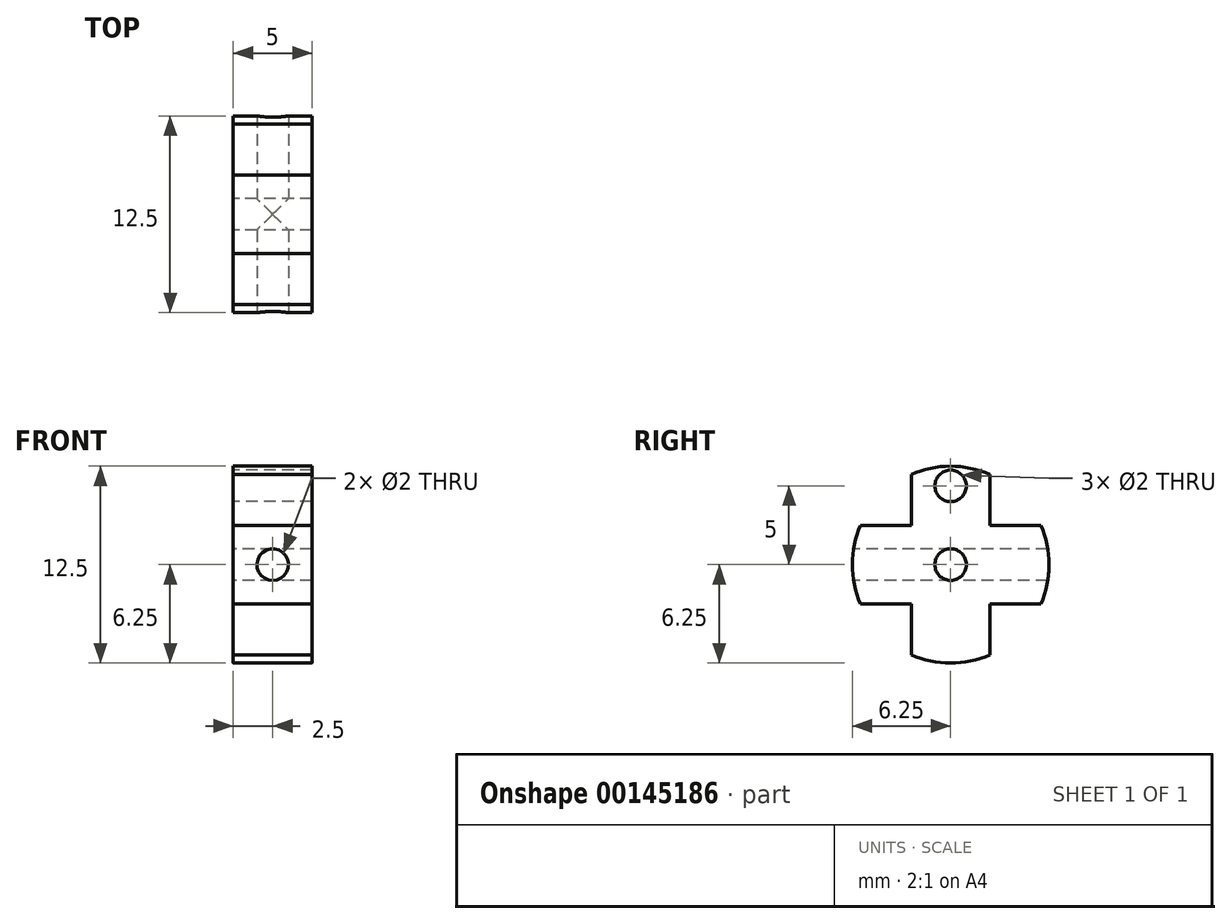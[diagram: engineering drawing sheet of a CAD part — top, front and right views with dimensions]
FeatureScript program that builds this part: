
annotation { "Feature Type Name" : "Feature", "Feature Type Description" : "" }
export const myFeature = defineFeature(function(context is Context, id is Id, definition is map)
    precondition{}
    {
        {
            var Q0;
            Q0=qCreatedBy(makeId("Right.planeOp"),FACE);
            var sketch = newSketch(context, id + "F0", { "sketchPlane" : qUnion([Q0])});
            skArc(sketch, "E0", {"start": v(-5.73, 2.5) * mm, "mid": v(-6.25, 0) * mm, "end": v(-5.73, -2.5) * mm});
            skLineSegment(sketch, "E1", {"start": v(-5.73, 2.5) * mm, "end": v(-2.5, 2.5) * mm});
            skLineSegment(sketch, "E2", {"start": v(-5.73, -2.5) * mm, "end": v(-2.5, -2.5) * mm});
            skLineSegment(sketch, "E3", {"start": v(-2.5, 5.73) * mm, "end": v(-2.5, 2.5) * mm});
            skLineSegment(sketch, "E4", {"start": v(2.5, 5.73) * mm, "end": v(2.5, 2.5) * mm});
            skCircle(sketch, "E5", {"center": v(0, 5) * mm, "radius": 1 * mm});
            skArc(sketch, "E6.trimOffspring", {"start": v(2.5, 5.73) * mm, "mid": v(0, 6.25) * mm, "end": v(-2.5, 5.73) * mm});
            skArc(sketch, "E7.trimOffspring", {"start": v(5.73, -2.5) * mm, "mid": v(6.25, 0) * mm, "end": v(5.73, 2.5) * mm});
            skArc(sketch, "E8.trimOffspring", {"start": v(-2.5, -5.73) * mm, "mid": v(0, -6.25) * mm, "end": v(2.5, -5.73) * mm});
            skLineSegment(sketch, "E9.trimOffspring", {"start": v(2.5, -2.5) * mm, "end": v(2.5, -5.73) * mm});
            skLineSegment(sketch, "E10.trimOffspring", {"start": v(2.5, 2.5) * mm, "end": v(8.52, 2.5) * mm});
            skLineSegment(sketch, "E11.trimOffspring", {"start": v(-2.5, -2.5) * mm, "end": v(-2.5, -5.73) * mm});
            skLineSegment(sketch, "E12.trimOffspring", {"start": v(2.5, -2.5) * mm, "end": v(10.46, -2.5) * mm});
            skCircle(sketch, "E13", {"center": v(0, 0) * mm, "radius": 1 * mm});
            skSolve(sketch);
        }
        {
            var Q0;
            Q0=makeQuery(id+"F0.imprint","IMPRINT",FACE,{"disambiguationData":[TD([[makeQuery(id+"F0.imprint","IMPRINT",EDGE,{"derivedFrom":sQuery(id+"F0.wireOp",EDGE,"E0")}),1.0]])]});
            extrude(context, id + "F1", {"entities" : qUnion([Q0]), "depth" : 5 * mm});
        }
        {
            var Q0;
            Q0=qCreatedBy(makeId("Front.planeOp"),FACE);
            var sketch = newSketch(context, id + "F2", { "sketchPlane" : qUnion([Q0])});
            skCircle(sketch, "E14", {"center": v(2.5, 0) * mm, "radius": 1 * mm});
            skSolve(sketch);
        }
        {
            var Q0;
            Q0 = qSketchRegion(id + "F2", true);
            extrude(context, id + "F3", {"entities" : qUnion([Q0]), "operationType" : NewBodyOperationType.REMOVE, "oppositeDirection" : true, "depth" : 25 * mm, "hasSecondDirection" : true, "secondDirectionOppositeDirection" : false, "secondDirectionDepth" : 25 * mm});
        }
    });
